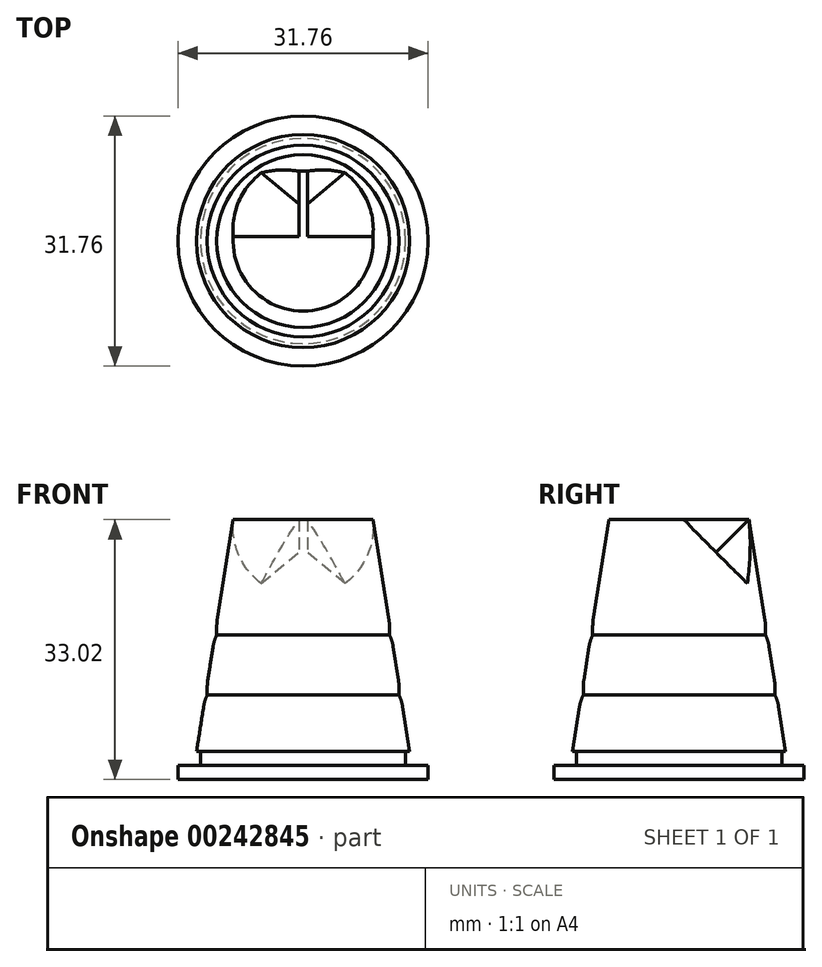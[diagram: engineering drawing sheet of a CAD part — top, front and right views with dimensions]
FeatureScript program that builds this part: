
annotation { "Feature Type Name" : "Feature", "Feature Type Description" : "" }
export const myFeature = defineFeature(function(context is Context, id is Id, definition is map)
    precondition{}
    {
        {
            var Q0;
            Q0=qCreatedBy(makeId("Front.planeOp"),FACE);
            var sketch = newSketch(context, id + "F0", { "sketchPlane" : qUnion([Q0])});
            skLineSegment(sketch, "E0", {"start": v(0, 16.51) * mm, "end": v(0, -16.51) * mm});
            skLineSegment(sketch, "E1", {"start": v(0, -16.51) * mm, "end": v(14.1, -16.51) * mm});
            skLineSegment(sketch, "E2", {"start": v(14.1, -16.51) * mm, "end": v(0, 16.51) * mm, "construction": true});
            skLineSegment(sketch, "E3", {"start": v(0, 16.51) * mm, "end": v(8.9, 16.51) * mm});
            skLineSegment(sketch, "E4", {"start": v(8.9, 16.51) * mm, "end": v(10.97, 3.3) * mm});
            skLineSegment(sketch, "E5", {"start": v(0, -6.35) * mm, "end": v(12.5, -6.35) * mm});
            skLineSegment(sketch, "E6", {"start": v(0, 1.27) * mm, "end": v(11.3, 1.27) * mm});
            skLineSegment(sketch, "E7", {"start": v(0, -4.32) * mm, "end": v(12.17, -4.32) * mm});
            skLineSegment(sketch, "E8", {"start": v(0, 3.3) * mm, "end": v(10.97, 3.3) * mm});
            skLineSegment(sketch, "E9", {"start": v(10.97, 3.3) * mm, "end": v(10.97, 1.83) * mm});
            skLineSegment(sketch, "E10", {"start": v(12.17, -4.32) * mm, "end": v(12.17, -5.8) * mm});
            skLineSegment(sketch, "E11", {"start": v(12.5, -6.35) * mm, "end": v(12.17, -5.8) * mm});
            skLineSegment(sketch, "E12", {"start": v(11.3, 1.27) * mm, "end": v(10.97, 1.83) * mm});
            skLineSegment(sketch, "E13.trimOffspring", {"start": v(11.3, 1.27) * mm, "end": v(12.17, -4.32) * mm});
            skLineSegment(sketch, "E14.trimOffspring", {"start": v(12.5, -6.35) * mm, "end": v(14.1, -16.51) * mm});
            skSolve(sketch);
        }
        {
            var Q0;
            Q0 = qSketchRegion(id + "F0", true);
            var Q1;
            Q1=sQuery(id+"F0.wireOp",EDGE,"E0");
            revolve(context, id + "F1", {"entities" : qUnion([Q0]), "axis" : qUnion([Q1]), "revolveType" : RevolveType.FULL});
        }
        {
            var Q0;
            Q0=makeQuery(id+"F1.opRevolve","SWEPT_FACE",FACE,{"disambiguationData":[OSD([sQuery(id+"F0.wireOp",EDGE,"E1")])]});
            var sketch = newSketch(context, id + "F2", { "sketchPlane" : qUnion([Q0])});
            skCircle(sketch, "E15", {"center": v(0, 0) * mm, "radius": 15.88 * mm});
            skSolve(sketch);
        }
        {
            var Q0;
            Q0 = qSketchRegion(id + "F2", true);
            extrude(context, id + "F3", {"entities" : qUnion([Q0]), "operationType" : NewBodyOperationType.ADD, "oppositeDirection" : true, "depth" : 1.78 * mm});
        }
        {
            var Q0;
            Q0=qCreatedBy(makeId("Front.planeOp"),FACE);
            var sketch = newSketch(context, id + "F4", { "sketchPlane" : qUnion([Q0])});
            skLineSegment(sketch, "E16", {"start": v(13.92, -12.95) * mm, "end": v(13.03, -12.95) * mm});
            skLineSegment(sketch, "E17", {"start": v(13.03, -12.95) * mm, "end": v(13.03, -14.73) * mm});
            skLineSegment(sketch, "E18", {"start": v(13.03, -14.73) * mm, "end": v(13.92, -14.73) * mm});
            skLineSegment(sketch, "E19", {"start": v(13.92, -14.73) * mm, "end": v(13.92, -12.95) * mm});
            skLineSegment(sketch, "E20", {"start": v(0, 0) * mm, "end": v(0, -16.4) * mm, "construction": true});
            skSolve(sketch);
        }
        {
            var Q0;
            Q0 = qSketchRegion(id + "F4", true);
            var Q1;
            Q1=sQuery(id+"F4.wireOp",EDGE,"E20");
            revolve(context, id + "F5", {"operationType" : NewBodyOperationType.REMOVE, "entities" : qUnion([Q0]), "axis" : qUnion([Q1]), "revolveType" : RevolveType.FULL, "oppositeDirection" : true});
        }
        {
            var Q0;
            Q0=makeQuery(id+"F1.opRevolve","SWEPT_EDGE",EDGE,{"disambiguationData":[OSD([sQuery(id+"F0.wireOp",EDGE,"E7"),sQuery(id+"F0.wireOp",EDGE,"E10"),sQuery(id+"F0.wireOp",EDGE,"E13.trimOffspring")])]});
            var Q1;
            Q1=makeQuery(id+"F1.opRevolve","SWEPT_EDGE",EDGE,{"disambiguationData":[OSD([sQuery(id+"F0.wireOp",EDGE,"E4"),sQuery(id+"F0.wireOp",EDGE,"E8"),sQuery(id+"F0.wireOp",EDGE,"E9")])]});
            fillet(context, id + "F6", {"entities" : qUnion([Q0, Q1]), "radius" : 5.08 * mm, "tangentPropagation" : true, "allowEdgeOverflow" : false});
        }
        {
            var Q0;
            Q0=makeQuery(id+"F1.opRevolve","SWEPT_EDGE",EDGE,{"disambiguationData":[OSD([sQuery(id+"F0.wireOp",EDGE,"E6"),sQuery(id+"F0.wireOp",EDGE,"E12"),sQuery(id+"F0.wireOp",EDGE,"E13.trimOffspring")])]});
            var Q1;
            Q1=makeQuery(id+"F1.opRevolve","SWEPT_EDGE",EDGE,{"disambiguationData":[OSD([sQuery(id+"F0.wireOp",EDGE,"E5"),sQuery(id+"F0.wireOp",EDGE,"E11"),sQuery(id+"F0.wireOp",EDGE,"E14.trimOffspring")])]});
            fillet(context, id + "F7", {"entities" : qUnion([Q0, Q1]), "radius" : 5.08 * mm, "tangentPropagation" : true, "allowEdgeOverflow" : false});
        }
        {
            var Q0;
            Q0=makeQuery(id+"F1.opRevolve","SWEPT_FACE",FACE,{"disambiguationData":[OSD([sQuery(id+"F0.wireOp",EDGE,"E3")])]});
            var sketch = newSketch(context, id + "F8", { "sketchPlane" : qUnion([Q0])});
            skLineSegment(sketch, "E21", {"start": v(0, 8.9) * mm, "end": v(0, -8.9) * mm});
            skLineSegment(sketch, "E22", {"start": v(0.54, 8.87) * mm, "end": v(0.54, -8.87) * mm});
            skLineSegment(sketch, "E23", {"start": v(-0.54, 8.87) * mm, "end": v(-0.54, -8.87) * mm});
            skLineSegment(sketch, "E24", {"start": v(-8.9, 0) * mm, "end": v(8.9, 0) * mm});
            skLineSegment(sketch, "E25", {"start": v(-8.87, 0.54) * mm, "end": v(8.87, 0.54) * mm});
            skLineSegment(sketch, "E26", {"start": v(-8.87, -0.54) * mm, "end": v(8.87, -0.54) * mm});
            skSolve(sketch);
        }
        {
            var Q0;
            Q0=qCreatedBy(makeId("Front.planeOp"),FACE);
            var Q1;
            Q1=sQuery(id+"F8.wireOp",EDGE,"E25");
            cPlane(context, id + "F9", {"entities" : qUnion([Q0, Q1]), "cplaneType" : CPlaneType.LINE_ANGLE, "offset" : 25.4 * mm, "angle" : 45 * degree, "width" : 152.4 * mm, "height" : 152.4 * mm});
        }
        {
            var Q0;
            Q0=qCreatedBy(makeId("Front.planeOp"),FACE);
            var Q1;
            Q1=sQuery(id+"F8.wireOp",EDGE,"E26");
            cPlane(context, id + "F10", {"entities" : qUnion([Q0, Q1]), "cplaneType" : CPlaneType.LINE_ANGLE, "offset" : 25.4 * mm, "angle" : 45 * degree, "oppositeDirection" : true, "width" : 152.4 * mm, "height" : 152.4 * mm});
        }
        {
            var Q0;
            Q0=qCreatedBy(id+"F9.planeOp",FACE);
            var sketch = newSketch(context, id + "F11", { "sketchPlane" : qUnion([Q0])});
            skLineSegment(sketch, "E27", {"start": v(0.54, 11.3) * mm, "end": v(8.87, 11.3) * mm});
            skLineSegment(sketch, "E28", {"start": v(-0.54, 11.3) * mm, "end": v(-8.87, 11.3) * mm});
            skLineSegment(sketch, "E29", {"start": v(-4.7, 11.3) * mm, "end": v(-4.7, -2.9) * mm, "construction": true});
            skLineSegment(sketch, "E30", {"start": v(4.7, 11.3) * mm, "end": v(4.7, -2.9) * mm, "construction": true});
            skLineSegment(sketch, "E31", {"start": v(-8.87, 4.2) * mm, "end": v(8.87, 4.2) * mm, "construction": true});
            skPoint(sketch, "E31.startSnap0", {"position": v(-4.7, 4.2) * mm});
            skLineSegment(sketch, "E32", {"start": v(-7.62, -2.9) * mm, "end": v(7.62, -2.9) * mm, "construction": true});
            skLineSegment(sketch, "E33", {"start": v(0, 0) * mm, "end": v(0, -2.9) * mm, "construction": true});
            skFitSpline(sketch, "E34", {"points": [v(8.87, 11.3) * mm, v(8.87, 4.2) * mm, v(7.62, -2.9) * mm], "startDerivative": vector(0.4, -15.45) * mm, "endDerivative": vector(-1.98, -15.39) * mm});
            skFitSpline(sketch, "E35", {"points": [v(-8.87, 11.3) * mm, v(-8.87, 4.2) * mm, v(-7.62, -2.9) * mm], "startDerivative": vector(-0.4, -15.45) * mm, "endDerivative": vector(1.98, -15.39) * mm});
            skLineSegment(sketch, "E36", {"start": v(7.62, -2.9) * mm, "end": v(0.54, 5.4) * mm});
            skLineSegment(sketch, "E37", {"start": v(-7.62, -2.9) * mm, "end": v(-0.54, 5.4) * mm});
            skLineSegment(sketch, "E38", {"start": v(-0.54, 11.3) * mm, "end": v(-0.54, 5.4) * mm});
            skLineSegment(sketch, "E39", {"start": v(0.54, 5.4) * mm, "end": v(0.54, 11.3) * mm});
            skLineSegment(sketch, "E40", {"start": v(-0.54, 11.3) * mm, "end": v(-7.62, -2.9) * mm, "construction": true});
            skLineSegment(sketch, "E41", {"start": v(0.54, 11.3) * mm, "end": v(7.62, -2.9) * mm, "construction": true});
            skSolve(sketch);
        }
        {
            var Q0;
            Q0 = qSketchRegion(id + "F11", true);
            extrude(context, id + "F12", {"entities" : qUnion([Q0]), "operationType" : NewBodyOperationType.REMOVE, "depth" : 25.4 * mm});
        }
    });
